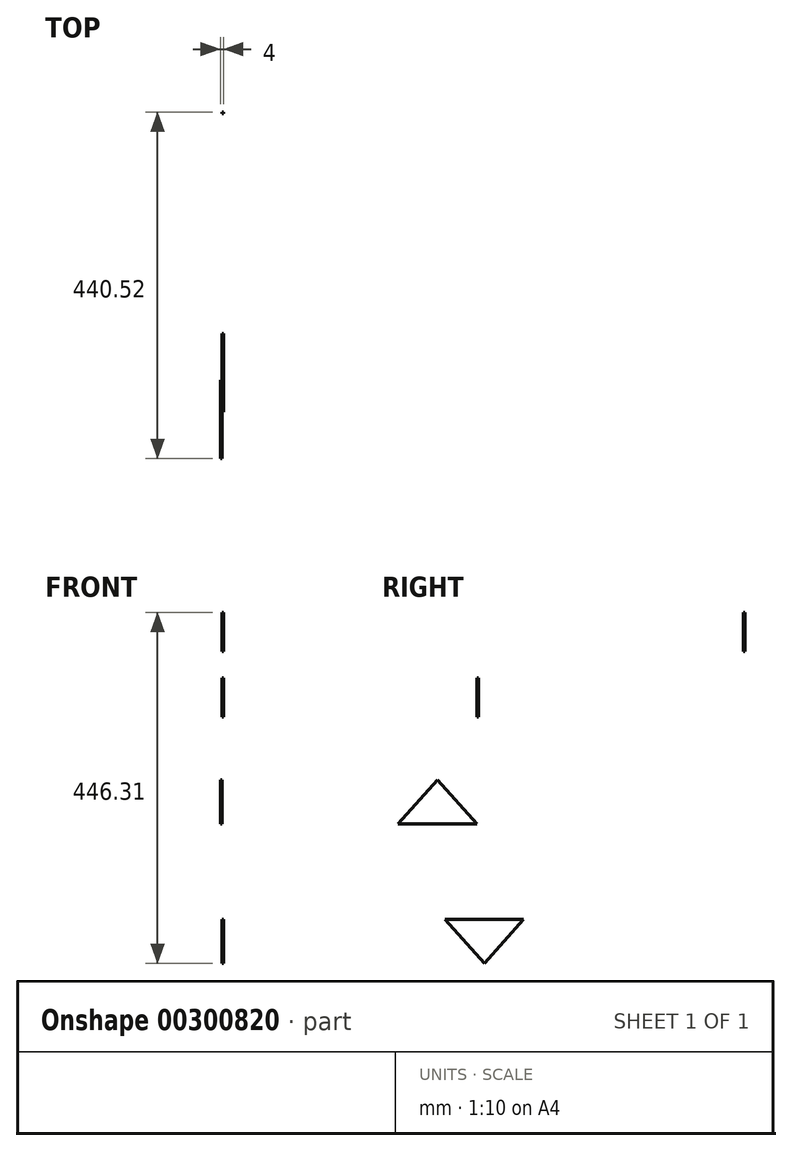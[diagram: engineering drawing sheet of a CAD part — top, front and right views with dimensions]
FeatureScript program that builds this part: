
annotation { "Feature Type Name" : "Feature", "Feature Type Description" : "" }
export const myFeature = defineFeature(function(context is Context, id is Id, definition is map)
    precondition{}
    {
        {
            var Q0;
            Q0=qCreatedBy(makeId("Right.planeOp"),FACE);
            var sketch = newSketch(context, id + "F0", { "sketchPlane" : qUnion([Q0])});
            skLineSegment(sketch, "E0", {"start": v(0, 0) * mm, "end": v(-100, 0) * mm});
            skLineSegment(sketch, "E1", {"start": v(-100, 0) * mm, "end": v(-50, 55.9) * mm});
            skLineSegment(sketch, "E2", {"start": v(-50, 55.9) * mm, "end": v(0, 0) * mm});
            skSolve(sketch);
        }
        {
            var Q0;
            Q0=makeQuery(id+"F0.imprint","IMPRINT",FACE,{"disambiguationData":[TD([[makeQuery(id+"F0.imprint","IMPRINT",EDGE,{"derivedFrom":sQuery(id+"F0.wireOp",EDGE,"E0")}),-1.0]])]});
            extrude(context, id + "F1", {"entities" : qUnion([Q0]), "oppositeDirection" : true, "depth" : 2 * mm});
        }
        {
            var Q0;
            Q0=qCreatedBy(makeId("Right.planeOp"),FACE);
            var sketch = newSketch(context, id + "F2", { "sketchPlane" : qUnion([Q0])});
            skPoint(sketch, "E3.0", {"position": v(0, 0) * mm});
            skLineSegment(sketch, "E4.bottom", {"start": v(2, 136) * mm, "end": v(0, 136) * mm});
            skLineSegment(sketch, "E4.top", {"start": v(2, 186) * mm, "end": v(0, 186) * mm});
            skLineSegment(sketch, "E4.left", {"start": v(2, 136) * mm, "end": v(2, 186) * mm});
            skLineSegment(sketch, "E4.right", {"start": v(0, 136) * mm, "end": v(0, 186) * mm});
            skSolve(sketch);
        }
        {
            var Q0;
            Q0=makeQuery(id+"F2.imprint","IMPRINT",FACE,{"disambiguationData":[TD([[makeQuery(id+"F2.imprint","IMPRINT",EDGE,{"derivedFrom":sQuery(id+"F2.wireOp",EDGE,"E4.bottom")}),-1.0]])]});
            extrude(context, id + "F3", {"entities" : qUnion([Q0]), "depth" : 2 * mm});
        }
        {
            var Q0;
            Q0=qCreatedBy(makeId("Right.planeOp"),FACE);
            var sketch = newSketch(context, id + "F4", { "sketchPlane" : qUnion([Q0])});
            skLineSegment(sketch, "E5", {"start": v(-40.67, -121.25) * mm, "end": v(59.33, -121.25) * mm});
            skLineSegment(sketch, "E6", {"start": v(-40.67, -121.25) * mm, "end": v(9.33, -177.15) * mm});
            skLineSegment(sketch, "E7", {"start": v(9.33, -177.15) * mm, "end": v(59.33, -121.25) * mm});
            skSolve(sketch);
        }
        {
            var Q0;
            Q0=makeQuery(id+"F4.imprint","IMPRINT",FACE,{"disambiguationData":[TD([[makeQuery(id+"F4.imprint","IMPRINT",EDGE,{"derivedFrom":sQuery(id+"F4.wireOp",EDGE,"E5")}),-1.0]])]});
            extrude(context, id + "F5", {"entities" : qUnion([Q0]), "depth" : 2 * mm});
        }
        {
            var Q0;
            Q0=qCreatedBy(makeId("Right.planeOp"),FACE);
            var sketch = newSketch(context, id + "F6", { "sketchPlane" : qUnion([Q0])});
            skLineSegment(sketch, "E8.bottom", {"start": v(338.52, 269.16) * mm, "end": v(340.52, 269.16) * mm});
            skLineSegment(sketch, "E8.top", {"start": v(338.52, 219.16) * mm, "end": v(340.52, 219.16) * mm});
            skLineSegment(sketch, "E8.left", {"start": v(338.52, 269.16) * mm, "end": v(338.52, 219.16) * mm});
            skLineSegment(sketch, "E8.right", {"start": v(340.52, 269.16) * mm, "end": v(340.52, 219.16) * mm});
            skSolve(sketch);
        }
        {
            var Q0;
            Q0=makeQuery(id+"F6.imprint","IMPRINT",FACE,{"disambiguationData":[TD([[makeQuery(id+"F6.imprint","IMPRINT",EDGE,{"derivedFrom":sQuery(id+"F6.wireOp",EDGE,"E8.bottom")}),-1.0]])]});
            extrude(context, id + "F7", {"entities" : qUnion([Q0]), "depth" : 2 * mm});
        }
    });
